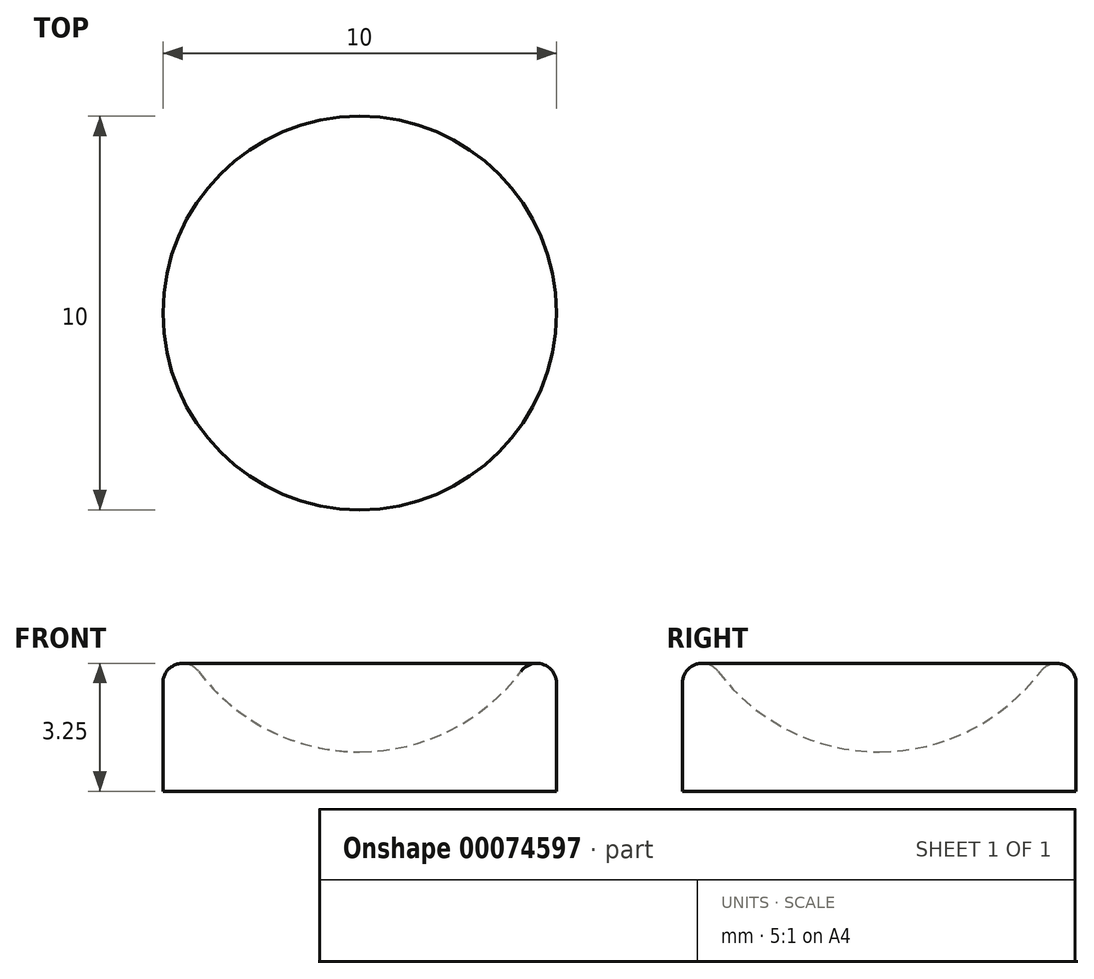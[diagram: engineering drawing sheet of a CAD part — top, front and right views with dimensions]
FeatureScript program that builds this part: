
annotation { "Feature Type Name" : "Feature", "Feature Type Description" : "" }
export const myFeature = defineFeature(function(context is Context, id is Id, definition is map)
    precondition{}
    {
        {
            var Q0;
            Q0=qCreatedBy(makeId("Front.planeOp"),FACE);
            var sketch = newSketch(context, id + "F0", { "sketchPlane" : qUnion([Q0])});
            skArc(sketch, "E0", {"start": v(0, 1) * mm, "mid": v(3.2, 2.12) * mm, "end": v(5, 5) * mm});
            skLineSegment(sketch, "E1", {"start": v(5, 5) * mm, "end": v(5, 0) * mm});
            skLineSegment(sketch, "E2", {"start": v(5, 0) * mm, "end": v(0, 0) * mm});
            skLineSegment(sketch, "E3", {"start": v(0, 0) * mm, "end": v(0, 1) * mm});
            skSolve(sketch);
        }
        {
            var Q0;
            Q0=makeQuery(id+"F0.imprint","IMPRINT",FACE,{"disambiguationData":[TD([[makeQuery(id+"F0.imprint","IMPRINT",EDGE,{"derivedFrom":sQuery(id+"F0.wireOp",EDGE,"E0")}),-1.0]])]});
            var Q1;
            Q1=sQuery(id+"F0.wireOp",EDGE,"E3");
            revolve(context, id + "F1", {"entities" : qUnion([Q0]), "axis" : qUnion([Q1]), "revolveType" : RevolveType.FULL});
        }
        {
            var Q0;
            Q0=makeQuery(id+"F1.opRevolve","SWEPT_EDGE",EDGE,{"disambiguationData":[OSD([sQuery(id+"F0.wireOp",EDGE,"E0"),sQuery(id+"F0.wireOp",EDGE,"E1")])]});
            fillet(context, id + "F2", {"entities" : qUnion([Q0]), "radius" : .5 * mm, "tangentPropagation" : true, "allowEdgeOverflow" : false});
        }
    });
